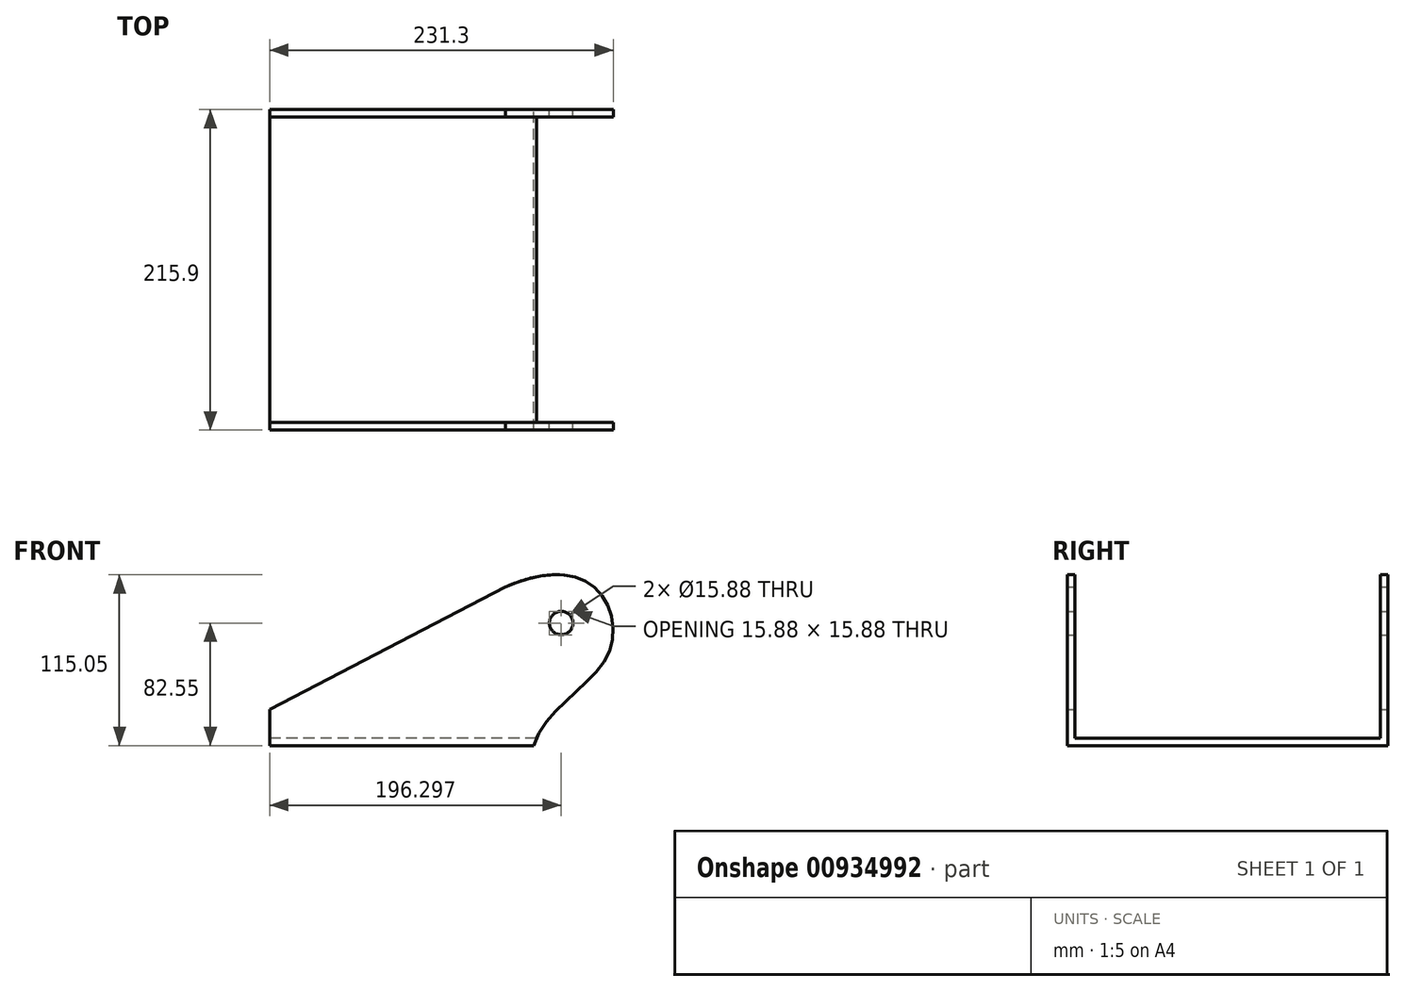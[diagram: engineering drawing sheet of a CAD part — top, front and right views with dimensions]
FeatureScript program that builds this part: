
annotation { "Feature Type Name" : "Feature", "Feature Type Description" : "" }
export const myFeature = defineFeature(function(context is Context, id is Id, definition is map)
    precondition{}
    {
        {
            var Q0;
            Q0=qCreatedBy(makeId("Front.planeOp"),FACE);
            var sketch = newSketch(context, id + "F0", { "sketchPlane" : qUnion([Q0])});
            skLineSegment(sketch, "E0", {"start": v(177.8, 0) * mm, "end": v(0, 0) * mm});
            skLineSegment(sketch, "E1", {"start": v(0, 0) * mm, "end": v(0, 24.26) * mm});
            skLineSegment(sketch, "E2", {"start": v(0, 24.26) * mm, "end": v(158.78, 106.75) * mm});
            skFitSpline(sketch, "E3", {"points": [v(158.78, 106.75) * mm, v(215.05, 109.32) * mm, v(228.03, 61.93) * mm, v(177.8, 0) * mm], "startDerivative": vector(163.64, 78.11) * mm, "endDerivative": vector(-57.8, -200.24) * mm});
            skCircle(sketch, "E4", {"center": v(196.3, 82.55) * mm, "radius": 7.94 * mm});
            skSolve(sketch);
        }
        {
            var Q0;
            Q0 = qSketchRegion(id + "F0", true);
            extrude(context, id + "F1", {"entities" : qUnion([Q0]), "depth" : 215.9 * mm, "offsetDistance" : 25.4 * mm});
        }
        {
            var Q0;
            Q0=qCreatedBy(makeId("Right.planeOp"),FACE);
            var sketch = newSketch(context, id + "F2", { "sketchPlane" : qUnion([Q0])});
            skLineSegment(sketch, "E5.bottom", {"start": v(-5.08, 150.4) * mm, "end": v(-210.82, 150.4) * mm});
            skLineSegment(sketch, "E5.top", {"start": v(-5.08, 5.08) * mm, "end": v(-210.82, 5.08) * mm});
            skLineSegment(sketch, "E5.left", {"start": v(-5.08, 150.4) * mm, "end": v(-5.08, 5.08) * mm});
            skLineSegment(sketch, "E5.right", {"start": v(-210.82, 150.4) * mm, "end": v(-210.82, 5.08) * mm});
            skSolve(sketch);
        }
        {
            var Q0;
            Q0 = qSketchRegion(id + "F2", true);
            extrude(context, id + "F3", {"entities" : qUnion([Q0]), "operationType" : NewBodyOperationType.REMOVE, "depth" : 508 * mm, "offsetDistance" : 25.4 * mm, "symmetric" : true});
        }
    });
